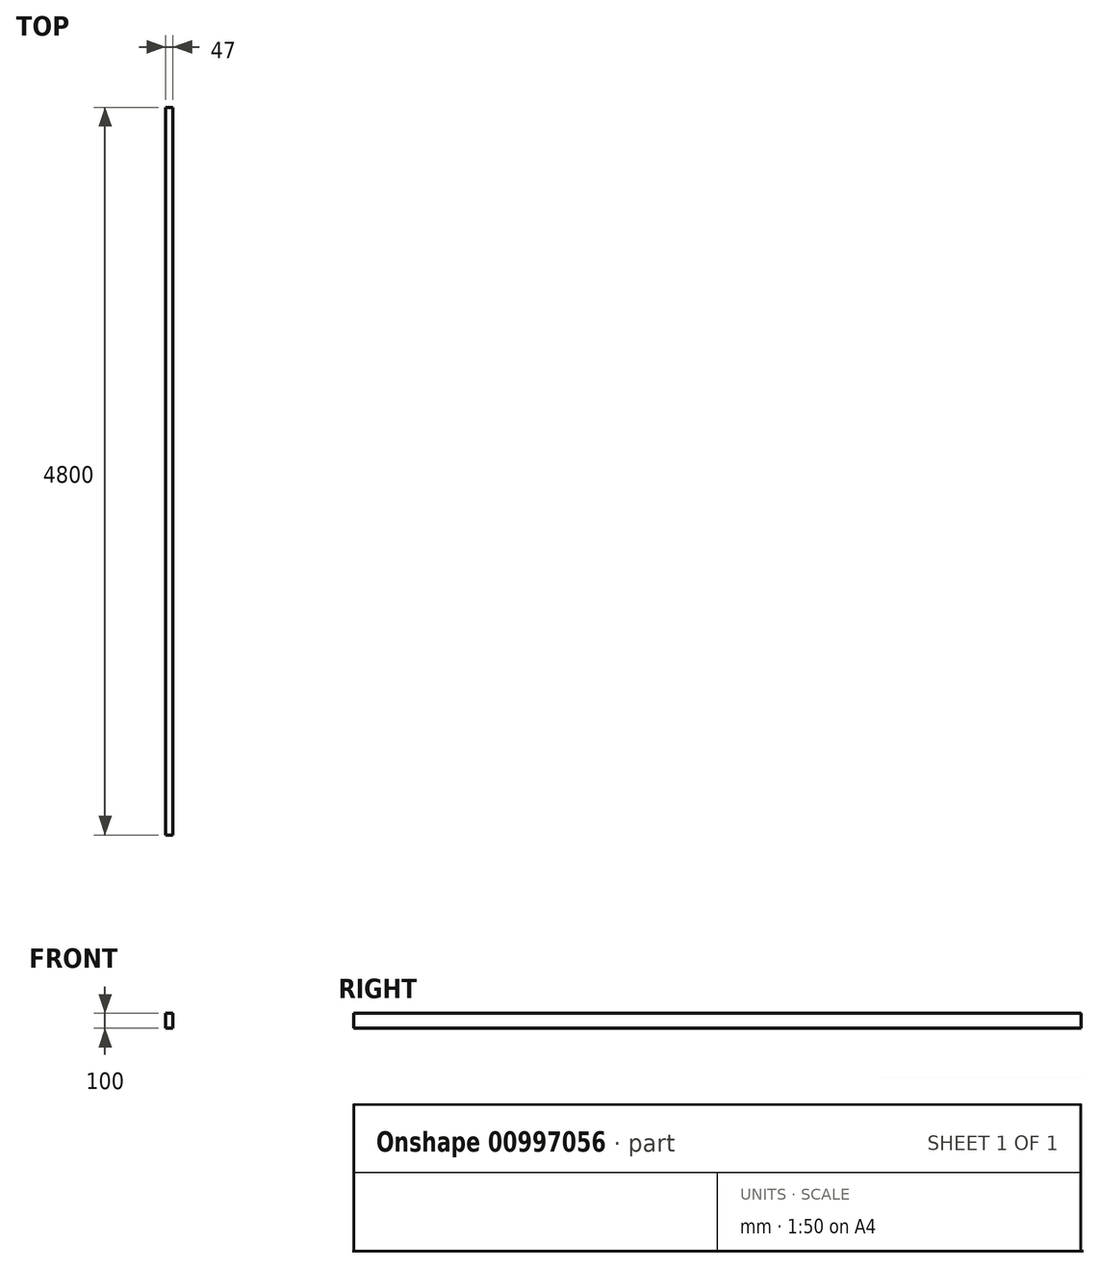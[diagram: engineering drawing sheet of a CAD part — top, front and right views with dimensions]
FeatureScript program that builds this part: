
annotation { "Feature Type Name" : "Feature", "Feature Type Description" : "" }
export const myFeature = defineFeature(function(context is Context, id is Id, definition is map)
    precondition{}
    {
        {
            var Q0;
            Q0=qCreatedBy(makeId("Front.planeOp"),FACE);
            var sketch = newSketch(context, id + "F0", { "sketchPlane" : qUnion([Q0])});
            skLineSegment(sketch, "E0.bottom", {"start": v(-81.24, 58.38) * mm, "end": v(-34.24, 58.38) * mm});
            skLineSegment(sketch, "E0.top", {"start": v(-81.24, -41.62) * mm, "end": v(-34.24, -41.62) * mm});
            skLineSegment(sketch, "E0.left", {"start": v(-81.24, 58.38) * mm, "end": v(-81.24, -41.62) * mm});
            skLineSegment(sketch, "E0.right", {"start": v(-34.24, 58.38) * mm, "end": v(-34.24, -41.62) * mm});
            skSolve(sketch);
        }
        {
            var Q0;
            Q0=makeQuery(id+"F0.imprint","IMPRINT",FACE,{"disambiguationData":[TD([[makeQuery(id+"F0.imprint","IMPRINT",EDGE,{"derivedFrom":sQuery(id+"F0.wireOp",EDGE,"E0.bottom")}),-1.0]])]});
            extrude(context, id + "F1", {"entities" : qUnion([Q0]), "oppositeDirection" : true, "depth" : 4800 * mm, "offsetDistance" : 25 * mm});
        }
    });
